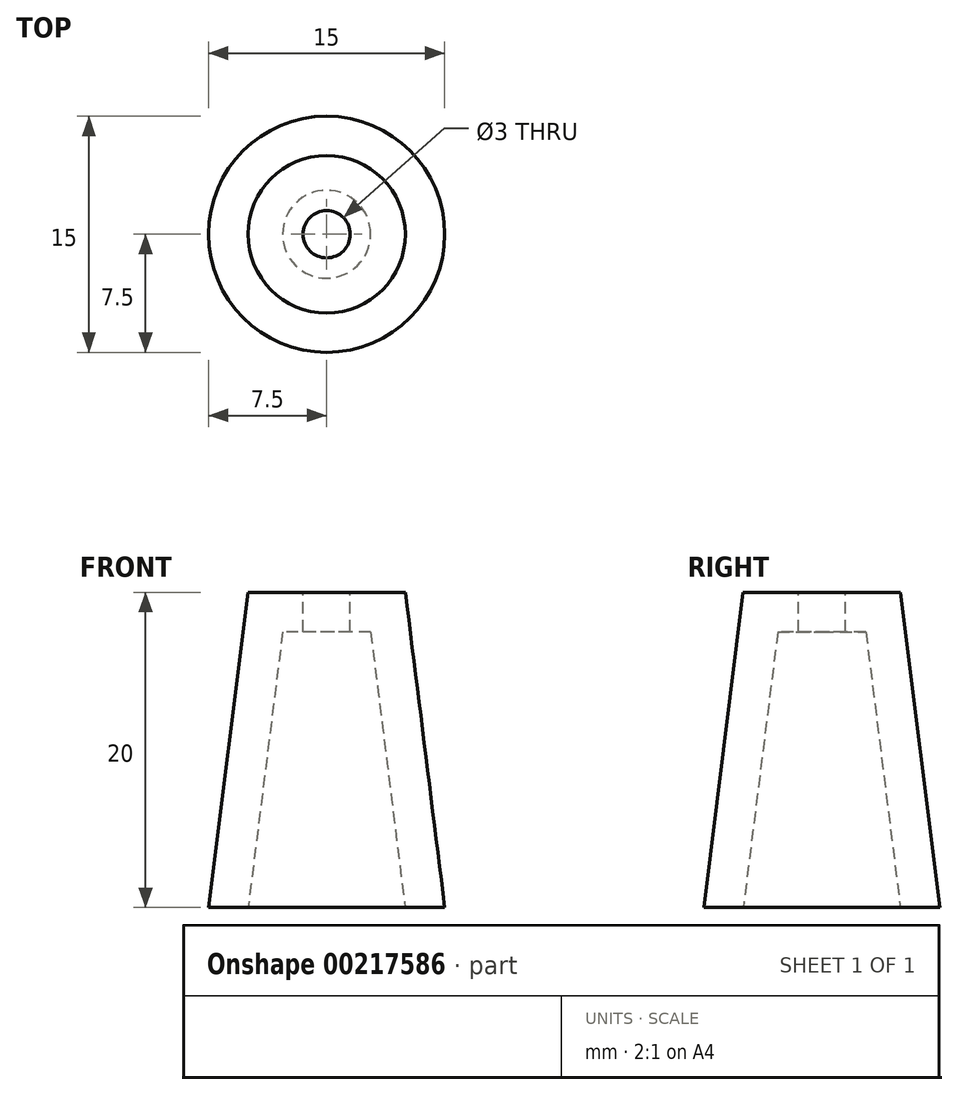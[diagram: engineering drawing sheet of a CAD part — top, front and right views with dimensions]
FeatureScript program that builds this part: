
annotation { "Feature Type Name" : "Feature", "Feature Type Description" : "" }
export const myFeature = defineFeature(function(context is Context, id is Id, definition is map)
    precondition{}
    {
        {
            var Q0;
            Q0=qCreatedBy(makeId("Top.planeOp"),FACE);
            var sketch = newSketch(context, id + "F0", { "sketchPlane" : qUnion([Q0])});
            skCircle(sketch, "E0", {"center": v(0, 0) * mm, "radius": 7.5 * mm});
            skSolve(sketch);
        }
        {
            var Q0;
            Q0=qCreatedBy(makeId("Top.planeOp"),FACE);
            cPlane(context, id + "F1", {"entities" : qUnion([Q0]), "cplaneType" : CPlaneType.OFFSET, "offset" : 20 * mm, "width" : 150 * mm, "height" : 150 * mm});
        }
        {
            var Q0;
            Q0=qCreatedBy(id+"F1.planeOp",FACE);
            var sketch = newSketch(context, id + "F2", { "sketchPlane" : qUnion([Q0])});
            skCircle(sketch, "E1", {"center": v(0, 0) * mm, "radius": 5 * mm});
            skSolve(sketch);
        }
        {
            var Q0;
            Q0=makeQuery(id+"F0.imprint","IMPRINT",FACE,{"disambiguationData":[TD([[makeQuery(id+"F0.imprint","IMPRINT",EDGE,{"derivedFrom":sQuery(id+"F0.wireOp",EDGE,"E0")}),1.0]])]});
            var Q1;
            Q1=makeQuery(id+"F2.imprint","IMPRINT",FACE,{"disambiguationData":[TD([[makeQuery(id+"F2.imprint","IMPRINT",EDGE,{"derivedFrom":sQuery(id+"F2.wireOp",EDGE,"E1")}),1.0]])]});
            var Q2;
            Q2=sQuery(id+"F0.wireOp",VERTEX,"E0.center");
            var Q3;
            Q3=sQuery(id+"F2.wireOp",VERTEX,"YKsnQJMt-z0hQ-Ixmz-QchP-bxnl9u2Qsdef.center");
            loft(context, id + "F3", {"sheetProfilesArray" : [{ "sheetProfileEntities" : qUnion([Q0]) }, { "sheetProfileEntities" : qUnion([Q1]) }], "connections" : [{ "connectionEntities" : qUnion([Q2, Q3]), "connectionEdgeQueries" : qUnion([]), "connectionEdgeParameters" : [] }]});
        }
        {
            var Q0;
            Q0=makeQuery(id+"F3.opLoft","CAP_FACE",FACE,{"disambiguationData":[OSD([makeQuery(id+"F0.imprint","IMPRINT",FACE,{"disambiguationData":[TD([[makeQuery(id+"F0.imprint","IMPRINT",EDGE,{"derivedFrom":sQuery(id+"F0.wireOp",EDGE,"E0")}),1.0]])]})])],"isStart":true});
            shell(context, id + "F4", {"entities" : qUnion([Q0]), "thickness" : 2.5 * mm});
        }
        {
            var Q0;
            Q0=makeQuery(id+"F3.opLoft","CAP_FACE",FACE,{"disambiguationData":[OSD([makeQuery(id+"F2.imprint","IMPRINT",FACE,{"disambiguationData":[TD([[makeQuery(id+"F2.imprint","IMPRINT",EDGE,{"derivedFrom":sQuery(id+"F2.wireOp",EDGE,"E1")}),1.0]])]})])],"isStart":true});
            var sketch = newSketch(context, id + "F5", { "sketchPlane" : qUnion([Q0])});
            skCircle(sketch, "E2", {"center": v(0, 0) * mm, "radius": 1.5 * mm});
            skSolve(sketch);
        }
        {
            var Q0;
            Q0=makeQuery(id+"F5.imprint","IMPRINT",FACE,{"disambiguationData":[TD([[makeQuery(id+"F5.imprint","IMPRINT",EDGE,{"derivedFrom":sQuery(id+"F5.wireOp",EDGE,"E2")}),1.0]])]});
            extrude(context, id + "F6", {"entities" : qUnion([Q0]), "operationType" : NewBodyOperationType.REMOVE, "oppositeDirection" : true, "depth" : 25 * mm});
        }
    });
